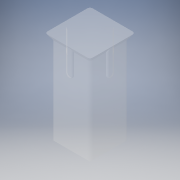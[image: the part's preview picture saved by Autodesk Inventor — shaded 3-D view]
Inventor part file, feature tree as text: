
AUTODESK INVENTOR PART (.ipt)
format: ipt  version: 2017 (Build 210142000, 142)  size: 296,448 bytes
history: native  units: mm
features: extrude x8, sketch x8, fillet x3, projected_geometry x3, chamfer x1
ambient origin geometry x8: Origin, YZ Plane, XZ Plane, XY Plane, X Axis, Y Axis, Z Axis, Center Point
bodies: Volumenkörper1 (feature_tree)
feature tree (23):
  extrude  "Extrusion1"  Depth=2.9mm
  extrude  "Extrusion2"  Depth=7.0mm
  extrude  "Extrusion3"  Depth=0.4mm TaperAngle=0.0deg
  extrude  "Extrusion4"  Depth=0.4mm TaperAngle=0.0deg
  chamfer  "Fase1"  Distance=0.5mm Angle=45.0deg
  extrude  "Extrusion5"  Depth=1.45mm
  extrude  "Extrusion6"  Depth=0.15mm TaperAngle=0.0deg
  extrude  "Extrusion7"  Depth=1.5mm
  extrude  "Extrusion8"  Depth=0.25mm TaperAngle=0.0deg
  fillet  "Rundung1"  Radius=0.1mm
  fillet  "Rundung2"  Radius=0.25mm
  fillet  "Rundung3"  Radius=0.25mm
  sketch  "Skizze1"  dims[d0=2.9mm d1=2.9mm]
  sketch  "Skizze2"  dims[d2=7.0mm d3=0.0mm d4=3.4mm]
  sketch  "Skizze3"  dims[d5=3.4mm d6=0.4mm d7=0.0mm]
  sketch  "Skizze4"  dims[d8=0.4mm d9=0.0mm d10=0.4mm d11=0.0mm d12=0.5mm d13=2.0mm d14=45.0deg]
  sketch  "Skizze5"  dims[d15=1.45mm d16=1.5mm]
  projected_geometry  "Projizierte Kontur1"
  sketch  "Skizze6"  dims[d17=0.5mm d18=0.15mm d19=0.0mm]
  projected_geometry  "Projizierte Kontur2"
  sketch  "Skizze7"  dims[d20=0.15mm d21=0.0mm d22=1.5mm d23=0.5mm]
  sketch  "Skizze8"  dims[d24=0.15mm d25=0.0mm d26=0.15mm d27=0.0mm d28=0.1mm d29=0.25mm d30=0.25mm]
  projected_geometry  "Projizierte Kontur3"
